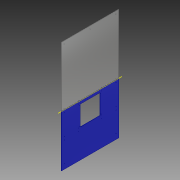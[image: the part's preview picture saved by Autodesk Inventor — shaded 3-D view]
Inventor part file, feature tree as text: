
AUTODESK INVENTOR PART (.ipt)
format: ipt  version: 2018 (Build 220112000, 112)  size: 151,040 bytes
history: native  units: in
note: dims shown in document units (in); Inventor stores cm internally (conversion verified against a paired STEP export)
features: plane x1, split x1, imported_body x1
ambient origin geometry x8: Origin, YZ Plane, XZ Plane, XY Plane, X Axis, Y Axis, Z Axis, Center Point
bodies: Solid1 (feature_tree), Solid2 (feature_tree), Solid3 (feature_tree)
feature tree (3):
  plane  "Work Plane1"
  split  "Split1"
  imported_body  "Imported1"
